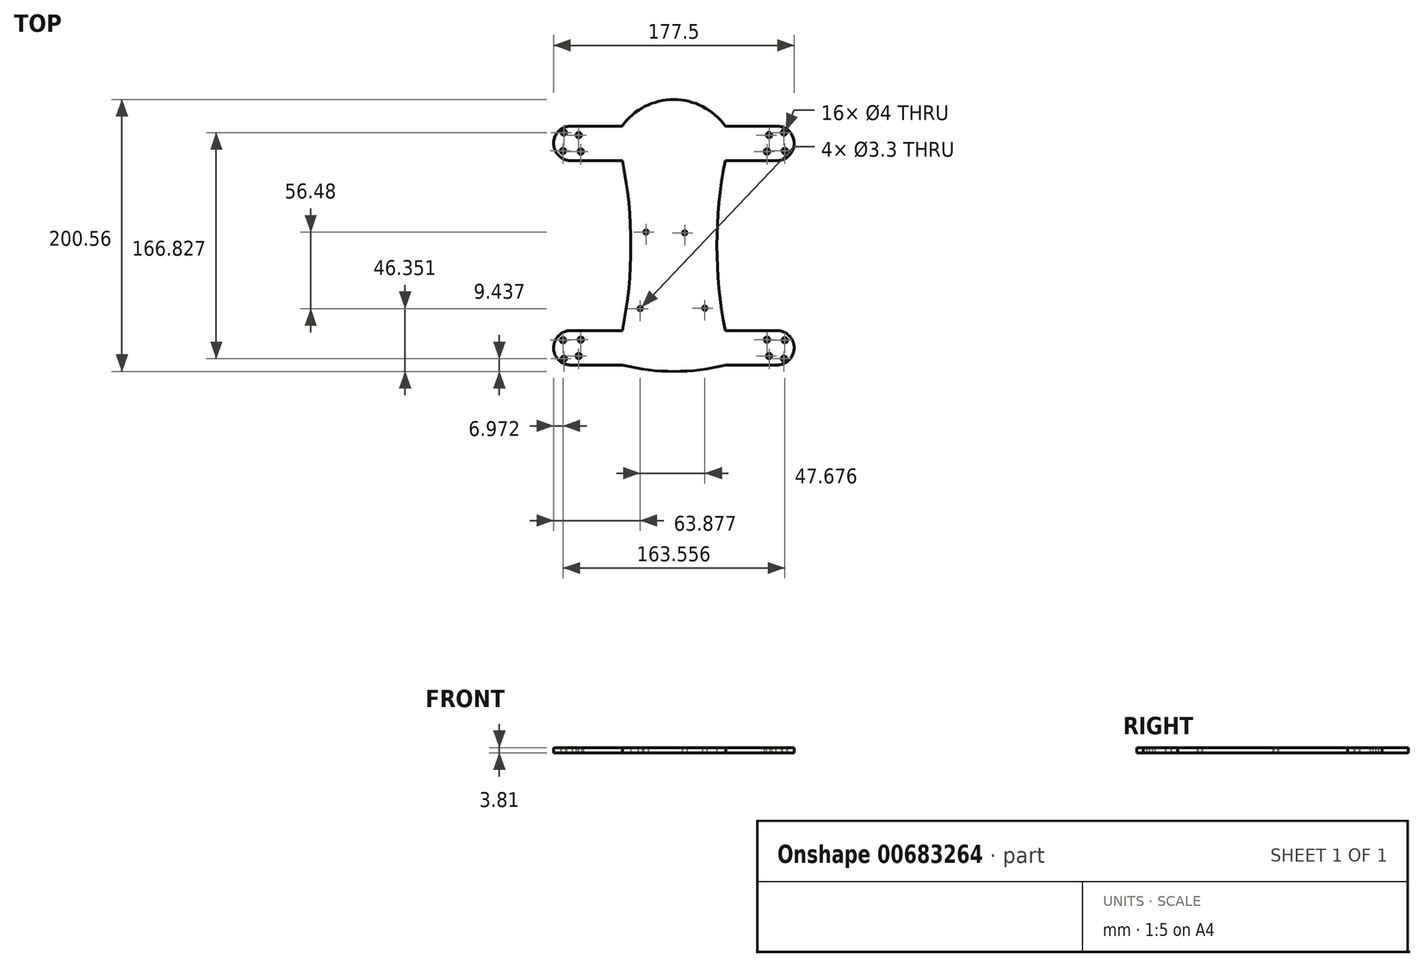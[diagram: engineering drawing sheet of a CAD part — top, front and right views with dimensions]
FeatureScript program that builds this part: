
annotation { "Feature Type Name" : "Feature", "Feature Type Description" : "" }
export const myFeature = defineFeature(function(context is Context, id is Id, definition is map)
    precondition{}
    {
        {
            var Q0;
            Q0=qCreatedBy(makeId("Top.planeOp"),FACE);
            var sketch = newSketch(context, id + "F0", { "sketchPlane" : qUnion([Q0])});
            skLineSegment(sketch, "E0.bottom", {"start": v(-38.25, 88.1) * mm, "end": v(37.95, 88.1) * mm});
            skLineSegment(sketch, "E0.top", {"start": v(-37.95, -88.1) * mm, "end": v(38.25, -88.1) * mm});
            skPoint(sketch, "E0.middle", {"position": v(0, 0) * mm});
            skLineSegment(sketch, "E1.bottom", {"start": v(37.95, 88.1) * mm, "end": v(76.05, 88.1) * mm});
            skLineSegment(sketch, "E1.top", {"start": v(37.95, 62.74) * mm, "end": v(74.97, 62.74) * mm});
            skLineSegment(sketch, "E1.left", {"start": v(37.95, 88.1) * mm, "end": v(37.95, 62.74) * mm});
            skArc(sketch, "E2", {"start": v(76.05, 88.1) * mm, "mid": v(88.74, 74.86) * mm, "end": v(74.97, 62.74) * mm});
            skLineSegment(sketch, "E3.left", {"start": v(38.25, -88.1) * mm, "end": v(37.95, -62.74) * mm});
            skArc(sketch, "E4.MirrorCS", {"start": v(-76.05, 88.1) * mm, "mid": v(-88.74, 74.86) * mm, "end": v(-74.97, 62.74) * mm});
            skLineSegment(sketch, "E5.MirrorCS", {"start": v(-37.95, 88.1) * mm, "end": v(-76.05, 88.1) * mm});
            skLineSegment(sketch, "E6.MirrorCS", {"start": v(-37.95, 62.74) * mm, "end": v(-74.97, 62.74) * mm});
            skCircle(sketch, "E7", {"center": v(-68.66, 69.38) * mm, "radius": 2 * mm});
            skCircle(sketch, "E8", {"center": v(-81.2, 83.41) * mm, "radius": 2 * mm});
            skCircle(sketch, "E9", {"center": v(-81.78, 69.82) * mm, "radius": 2 * mm});
            skCircle(sketch, "E10", {"center": v(-70.2, 81.49) * mm, "radius": 2 * mm});
            skCircle(sketch, "E11.MirrorC", {"center": v(70.2, 81.49) * mm, "radius": 2 * mm});
            skCircle(sketch, "E12.MirrorC", {"center": v(81.2, 83.41) * mm, "radius": 2 * mm});
            skCircle(sketch, "E13.MirrorC", {"center": v(81.78, 69.82) * mm, "radius": 2 * mm});
            skCircle(sketch, "E14.MirrorC", {"center": v(68.66, 69.38) * mm, "radius": 2 * mm});
            skArc(sketch, "E15", {"start": v(37.95, 88.1) * mm, "mid": v(-0.15, 107.71) * mm, "end": v(-38.25, 88.1) * mm});
            skArc(sketch, "E16", {"start": v(-37.95, -62.74) * mm, "mid": v(-31.75, 0) * mm, "end": v(-37.95, 62.74) * mm});
            skArc(sketch, "E17", {"start": v(37.95, 62.74) * mm, "mid": v(31.75, 0) * mm, "end": v(37.95, -62.74) * mm});
            skLineSegment(sketch, "E18", {"start": v(-38.25, 88.1) * mm, "end": v(-37.95, 62.74) * mm});
            skLineSegment(sketch, "E19", {"start": v(-37.95, -62.74) * mm, "end": v(-37.95, -88.1) * mm});
            skLineSegment(sketch, "E20.MirrorCS", {"start": v(-37.95, -88.1) * mm, "end": v(-76.05, -88.1) * mm});
            skLineSegment(sketch, "E21.MirrorCS", {"start": v(-37.95, -62.74) * mm, "end": v(-74.97, -62.74) * mm});
            skCircle(sketch, "E22.MirrorC", {"center": v(-68.66, -69.38) * mm, "radius": 2 * mm});
            skCircle(sketch, "E23.MirrorC", {"center": v(-70.2, -81.49) * mm, "radius": 2 * mm});
            skCircle(sketch, "E24.MirrorC", {"center": v(-81.2, -83.41) * mm, "radius": 2 * mm});
            skCircle(sketch, "E25.MirrorC", {"center": v(-81.78, -69.82) * mm, "radius": 2 * mm});
            skArc(sketch, "E26.MirrorCS", {"start": v(-76.05, -88.1) * mm, "mid": v(-88.74, -74.86) * mm, "end": v(-74.97, -62.74) * mm});
            skLineSegment(sketch, "E27.MirrorCS", {"start": v(37.95, -62.74) * mm, "end": v(74.97, -62.74) * mm});
            skLineSegment(sketch, "E28.MirrorCS", {"start": v(37.95, -88.1) * mm, "end": v(76.05, -88.1) * mm});
            skArc(sketch, "E29.MirrorCS", {"start": v(76.05, -88.1) * mm, "mid": v(88.74, -74.86) * mm, "end": v(74.97, -62.74) * mm});
            skCircle(sketch, "E30.MirrorC", {"center": v(70.2, -81.49) * mm, "radius": 2 * mm});
            skCircle(sketch, "E31.MirrorC", {"center": v(81.2, -83.41) * mm, "radius": 2 * mm});
            skCircle(sketch, "E32.MirrorC", {"center": v(81.78, -69.82) * mm, "radius": 2 * mm});
            skCircle(sketch, "E33.MirrorC", {"center": v(68.66, -69.38) * mm, "radius": 2 * mm});
            skCircle(sketch, "E34", {"center": v(-24.87, -46.5) * mm, "radius": 1.65 * mm});
            skLineSegment(sketch, "E35", {"start": v(-37.95, 62.74) * mm, "end": v(37.95, 62.74) * mm});
            skArc(sketch, "E36", {"start": v(-37.95, -88.1) * mm, "mid": v(0.15, -92.85) * mm, "end": v(38.25, -88.1) * mm});
            skLineSegment(sketch, "E37", {"start": v(-37.95, -62.74) * mm, "end": v(37.95, -62.74) * mm});
            skCircle(sketch, "E38", {"center": v(22.8, -46.14) * mm, "radius": 1.65 * mm});
            skCircle(sketch, "E39", {"center": v(-20.6, 9.98) * mm, "radius": 1.65 * mm});
            skCircle(sketch, "E40", {"center": v(7.98, 9.4) * mm, "radius": 1.65 * mm});
            skSolve(sketch);
        }
        {
            var Q0;
            Q0=makeQuery(id+"F0.imprint","IMPRINT",FACE,{"disambiguationData":[TD([[makeQuery(id+"F0.imprint","IMPRINT",EDGE,{"derivedFrom":sQuery(id+"F0.wireOp",EDGE,"E0.bottom")}),1.0]])]});
            var Q1;
            Q1=makeQuery(id+"F0.imprint","IMPRINT",FACE,{"disambiguationData":[TD([[makeQuery(id+"F0.imprint","IMPRINT",EDGE,{"derivedFrom":sQuery(id+"F0.wireOp",EDGE,"E0.bottom")}),-1.0]])]});
            var Q2;
            Q2=makeQuery(id+"F0.imprint","IMPRINT",FACE,{"disambiguationData":[TD([[makeQuery(id+"F0.imprint","IMPRINT",EDGE,{"derivedFrom":sQuery(id+"F0.wireOp",EDGE,"E4.MirrorCS")}),1.0]])]});
            var Q3;
            Q3=makeQuery(id+"F0.imprint","IMPRINT",FACE,{"disambiguationData":[TD([[makeQuery(id+"F0.imprint","IMPRINT",EDGE,{"derivedFrom":sQuery(id+"F0.wireOp",EDGE,"E1.bottom")}),-1.0]])]});
            var Q4;
            Q4=makeQuery(id+"F0.imprint","IMPRINT",FACE,{"disambiguationData":[TD([[makeQuery(id+"F0.imprint","IMPRINT",EDGE,{"derivedFrom":sQuery(id+"F0.wireOp",EDGE,"E19")}),-1.0]])]});
            var Q5;
            Q5=makeQuery(id+"F0.imprint","IMPRINT",FACE,{"disambiguationData":[TD([[makeQuery(id+"F0.imprint","IMPRINT",EDGE,{"derivedFrom":sQuery(id+"F0.wireOp",EDGE,"E3.left")}),-1.0]])]});
            var Q6;
            Q6=makeQuery(id+"F0.imprint","IMPRINT",FACE,{"disambiguationData":[TD([[makeQuery(id+"F0.imprint","IMPRINT",EDGE,{"derivedFrom":sQuery(id+"F0.wireOp",EDGE,"E0.top")}),1.0]])]});
            var Q7;
            Q7=makeQuery(id+"F0.imprint","IMPRINT",FACE,{"disambiguationData":[TD([[makeQuery(id+"F0.imprint","IMPRINT",EDGE,{"derivedFrom":sQuery(id+"F0.wireOp",EDGE,"E0.top")}),-1.0]])]});
            var Q8;
            Q8=makeQuery(id+"F0.imprint","IMPRINT",FACE,{"disambiguationData":[TD([[makeQuery(id+"F0.imprint","IMPRINT",EDGE,{"derivedFrom":sQuery(id+"F0.wireOp",EDGE,"E16")}),-1.0]])]});
            extrude(context, id + "F1", {"entities" : qUnion([Q0, Q1, Q2, Q3, Q4, Q5, Q6, Q7, Q8]), "depth" : 3.8 * mm, "offsetDistance" : 25.4 * mm});
        }
    });
